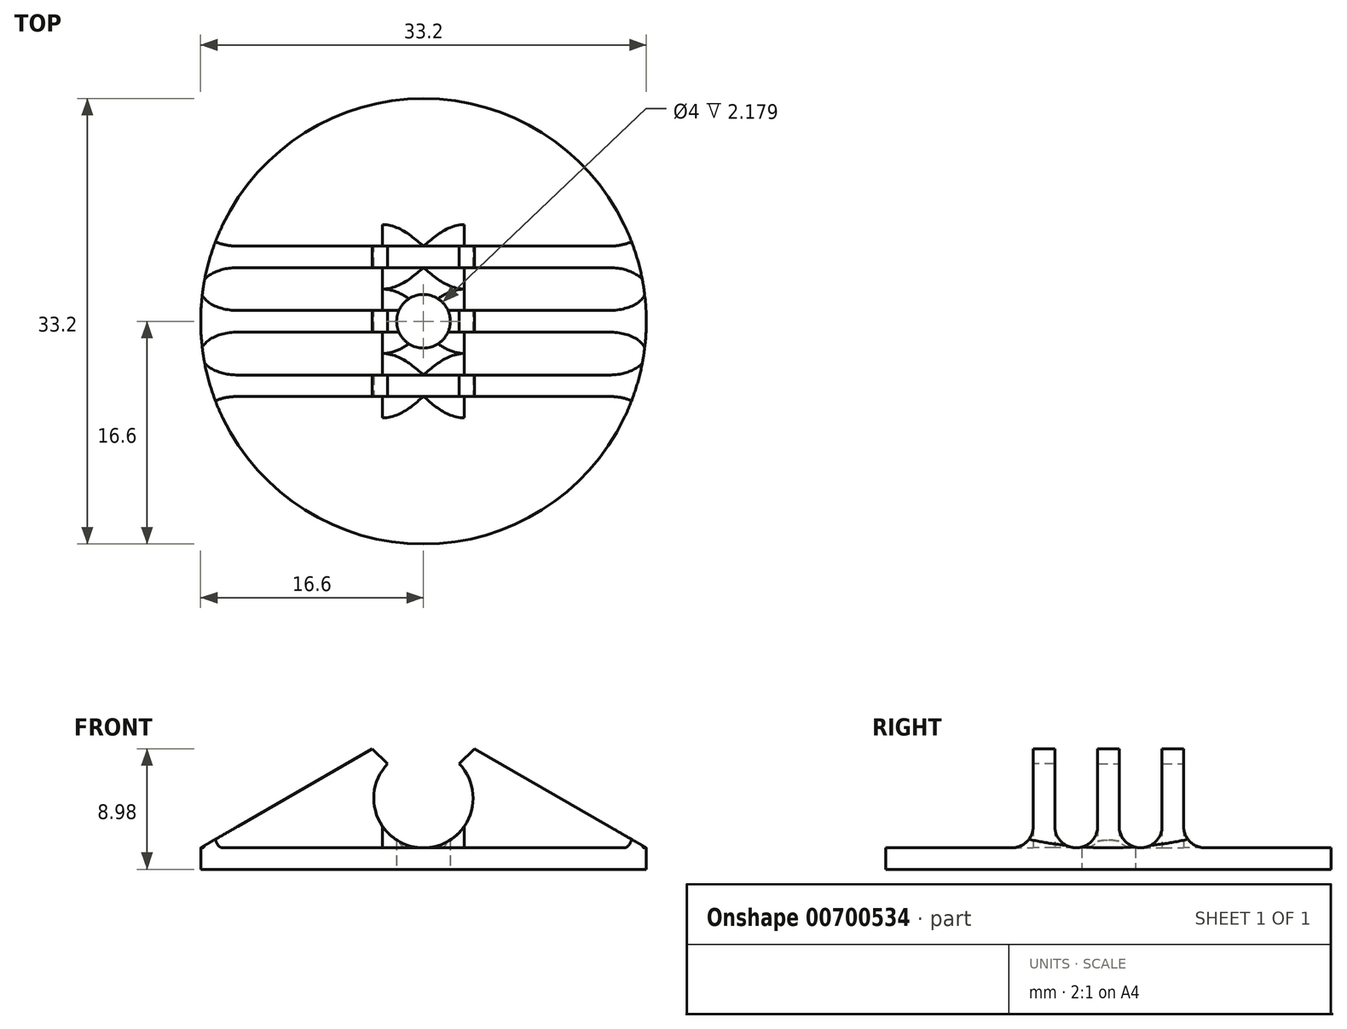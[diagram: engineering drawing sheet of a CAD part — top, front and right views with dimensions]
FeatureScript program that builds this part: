
annotation { "Feature Type Name" : "Feature", "Feature Type Description" : "" }
export const myFeature = defineFeature(function(context is Context, id is Id, definition is map)
    precondition{}
    {
        {
            assignVariable(context, id + "F0", {"name" : "Shells", "anyValue" : 2});
        }
        {
            assignVariable(context, id + "F1", {"name" : "Wall", "anyValue" : getVariable(context, 'Shells') * 2 * 0.4});
        }
        {
            var Q0;
            Q0=qCreatedBy(makeId("Front.planeOp"),FACE);
            var sketch = newSketch(context, id + "F2", { "sketchPlane" : qUnion([Q0])});
            skCircle(sketch, "E0", {"center": v(0, 5.3) * mm, "radius": 3.7 * mm});
            skLineSegment(sketch, "E1", {"start": v(-16.6, 0) * mm, "end": v(-16.6, 1.6) * mm});
            skLineSegment(sketch, "E2", {"start": v(-16.6, 1.6) * mm, "end": v(-3.81, 8.98) * mm});
            skLineSegment(sketch, "E3", {"start": v(-3.81, 8.98) * mm, "end": v(0, 5.3) * mm});
            skLineSegment(sketch, "E4", {"start": v(0, 5.3) * mm, "end": v(0, 0) * mm});
            skLineSegment(sketch, "E5", {"start": v(0, 0) * mm, "end": v(-16.6, 0) * mm});
            skLineSegment(sketch, "E6", {"start": v(-2.66, 7.87) * mm, "end": v(0, 10.63) * mm, "construction": true});
            skLineSegment(sketch, "E7", {"start": v(-16.6, 1.6) * mm, "end": v(0, 1.6) * mm});
            skSolve(sketch);
        }
        {
            var Q0;
            Q0=makeQuery(id+"F2.imprint","IMPRINT",FACE,{"disambiguationData":[TD([[makeQuery(id+"F2.imprint","IMPRINT",EDGE,{"derivedFrom":sQuery(id+"F2.wireOp",EDGE,"E1")}),-1.0]])]});
            var Q1;
            {var subQ4=sQuery(id+"F2.wireOp",EDGE,"E2");Q1=makeQuery(id+"F2.imprint","IMPRINT",FACE,{"disambiguationData":[TD([[makeQuery(id+"F2.imprint","IMPRINT",EDGE,{"derivedFrom":subQ4}),-1.0]])]});}
            extrude(context, id + "F3", {"entities" : qUnion([Q0, Q1]), "endBound" : BoundingType.SYMMETRIC, "depth" : (getVariable(context, 'Wall')) * mm, "offsetDistance" : 25 * mm});
        }
        {
            var Q0;
            Q0=makeQuery(id+"F2.imprint","IMPRINT",FACE,{"disambiguationData":[TD([[makeQuery(id+"F2.imprint","IMPRINT",EDGE,{"derivedFrom":sQuery(id+"F2.wireOp",EDGE,"E1")}),-1.0]])]});
            extrude(context, id + "F4", {"entities" : qUnion([Q0]), "operationType" : NewBodyOperationType.ADD, "endBound" : BoundingType.SYMMETRIC, "depth" : (getVariable(context, 'Wall') * 3) * mm, "offsetDistance" : 25 * mm});
        }
        {
            var Q0;
            Q0=makeQuery(id+"F3.opExtrude","SWEPT_BODY",BODY,{"disambiguationData":[OSD([sQuery(id+"F2.wireOp",EDGE,"E0"),sQuery(id+"F2.wireOp",EDGE,"E1"),sQuery(id+"F2.wireOp",EDGE,"E2"),sQuery(id+"F2.wireOp",EDGE,"E3"),sQuery(id+"F2.wireOp",EDGE,"E4"),sQuery(id+"F2.wireOp",EDGE,"E5")])]});
            var Q1;
            Q1=makeQuery(id+"F3.opExtrude","SWEPT_FACE",FACE,{"disambiguationData":[OSD([sQuery(id+"F2.wireOp",EDGE,"E4")])]});
            mirror(context, id + "F5", {"operationType" : NewBodyOperationType.ADD, "entities" : qUnion([Q0]), "mirrorPlane" : qUnion([Q1])});
        }
        {
            var Q0;
            Q0=makeQuery(id+"F5.opPattern","COPY",EDGE,{"derivedFrom":makeQuery(id+"F4.boolean.opBoolean","INTERSECT",EDGE,{"derivedFrom":[makeQuery(id+"F3.opExtrude","CAP_FACE",FACE,{"disambiguationData":[OSD([sQuery(id+"F2.wireOp",EDGE,"E0"),sQuery(id+"F2.wireOp",EDGE,"E1"),sQuery(id+"F2.wireOp",EDGE,"E2"),sQuery(id+"F2.wireOp",EDGE,"E3"),sQuery(id+"F2.wireOp",EDGE,"E4"),sQuery(id+"F2.wireOp",EDGE,"E5")])],"isStart":true}),makeQuery(id+"F4.opExtrude","SWEPT_FACE",FACE,{"disambiguationData":[OSD([sQuery(id+"F2.wireOp",EDGE,"E7")])]})]}),"instanceName":"1"});
            var Q1;
            Q1=makeQuery(id+"F4.boolean.opBoolean","INTERSECT",EDGE,{"derivedFrom":[makeQuery(id+"F3.opExtrude","CAP_FACE",FACE,{"disambiguationData":[OSD([sQuery(id+"F2.wireOp",EDGE,"E0"),sQuery(id+"F2.wireOp",EDGE,"E1"),sQuery(id+"F2.wireOp",EDGE,"E2"),sQuery(id+"F2.wireOp",EDGE,"E3"),sQuery(id+"F2.wireOp",EDGE,"E4"),sQuery(id+"F2.wireOp",EDGE,"E5")])],"isStart":false}),makeQuery(id+"F4.opExtrude","SWEPT_FACE",FACE,{"disambiguationData":[OSD([sQuery(id+"F2.wireOp",EDGE,"E7")])]})]});
            fillet(context, id + "F6", {"entities" : qUnion([Q0, Q1]), "radius" : (getVariable(context, 'Wall')) * mm, "tangentPropagation" : true, "allowEdgeOverflow" : false});
        }
        {
            var Q0;
            Q0=makeQuery(id+"F3.opExtrude","SWEPT_BODY",BODY,{"disambiguationData":[OSD([sQuery(id+"F2.wireOp",EDGE,"E0"),sQuery(id+"F2.wireOp",EDGE,"E1"),sQuery(id+"F2.wireOp",EDGE,"E2"),sQuery(id+"F2.wireOp",EDGE,"E3"),sQuery(id+"F2.wireOp",EDGE,"E4"),sQuery(id+"F2.wireOp",EDGE,"E5")])]});
            var Q1;
            {var subQ0=makeQuery(id+"F4.opExtrude","CAP_FACE",FACE,{"disambiguationData":[OSD([sQuery(id+"F2.wireOp",EDGE,"E1"),sQuery(id+"F2.wireOp",EDGE,"E4"),sQuery(id+"F2.wireOp",EDGE,"E5"),sQuery(id+"F2.wireOp",EDGE,"E7")])],"isStart":false});Q1=makeQuery(id+"F5.boolean.opBoolean","MERGE",FACE,{"derivedFrom":[subQ0,makeQuery(id+"F5.opPattern","COPY",FACE,{"derivedFrom":subQ0,"instanceName":"1"})]});}
            mirror(context, id + "F7", {"operationType" : NewBodyOperationType.ADD, "entities" : qUnion([Q0]), "mirrorPlane" : qUnion([Q1])});
        }
        {
            var Q0;
            Q0=makeQuery(id+"F3.opExtrude","SWEPT_BODY",BODY,{"disambiguationData":[OSD([sQuery(id+"F2.wireOp",EDGE,"E0"),sQuery(id+"F2.wireOp",EDGE,"E1"),sQuery(id+"F2.wireOp",EDGE,"E2"),sQuery(id+"F2.wireOp",EDGE,"E3"),sQuery(id+"F2.wireOp",EDGE,"E4"),sQuery(id+"F2.wireOp",EDGE,"E5")])]});
            var Q1;
            Q1=qCreatedBy(makeId("Front.planeOp"),FACE);
            mirror(context, id + "F8", {"operationType" : NewBodyOperationType.ADD, "entities" : qUnion([Q0]), "mirrorPlane" : qUnion([Q1])});
        }
        {
            var Q0;
            Q0=qCreatedBy(makeId("Top.planeOp"),FACE);
            var sketch = newSketch(context, id + "F9", { "sketchPlane" : qUnion([Q0])});
            skCircle(sketch, "E8", {"center": v(0, 0) * mm, "radius": 16.6 * mm});
            skSolve(sketch);
        }
        {
            var Q0;
            Q0=makeQuery(id+"F9.imprint","IMPRINT",FACE,{"disambiguationData":[TD([[makeQuery(id+"F9.imprint","IMPRINT",EDGE,{"derivedFrom":sQuery(id+"F9.wireOp",EDGE,"E8")}),1.0]])]});
            extrude(context, id + "F10", {"entities" : qUnion([Q0]), "operationType" : NewBodyOperationType.INTERSECT, "depth" : 25 * mm, "offsetDistance" : 25 * mm});
        }
        {
            var Q0;
            Q0=makeQuery(id+"F9.imprint","IMPRINT",FACE,{"disambiguationData":[TD([[makeQuery(id+"F9.imprint","IMPRINT",EDGE,{"derivedFrom":sQuery(id+"F9.wireOp",EDGE,"E8")}),1.0]])]});
            extrude(context, id + "F11", {"entities" : qUnion([Q0]), "operationType" : NewBodyOperationType.ADD, "depth" : (getVariable(context, 'Wall')) * mm, "offsetDistance" : 25 * mm});
        }
        {
            var Q0;
            Q0=sQuery(id+"F9.wireOp",VERTEX,"E8.center");
            var Q1;
            Q1=makeQuery(id+"F3.opExtrude","SWEPT_BODY",BODY,{"disambiguationData":[OSD([sQuery(id+"F2.wireOp",EDGE,"E0"),sQuery(id+"F2.wireOp",EDGE,"E1"),sQuery(id+"F2.wireOp",EDGE,"E2"),sQuery(id+"F2.wireOp",EDGE,"E3"),sQuery(id+"F2.wireOp",EDGE,"E4"),sQuery(id+"F2.wireOp",EDGE,"E5")])]});
            hole(context, id + "F12", {"style" : HoleStyle.SIMPLE, "endStyle" : HoleEndStyle.THROUGH, "oppositeDirection" : true, "holeDiameter" : 4 * mm, "majorDiameter" : 5 * mm, "isTappedThrough" : true, "tappedDepth" : 12 * mm, "tapClearance" : 3, "locations" : qUnion([Q0]), "scope" : qUnion([Q1])});
        }
    });
